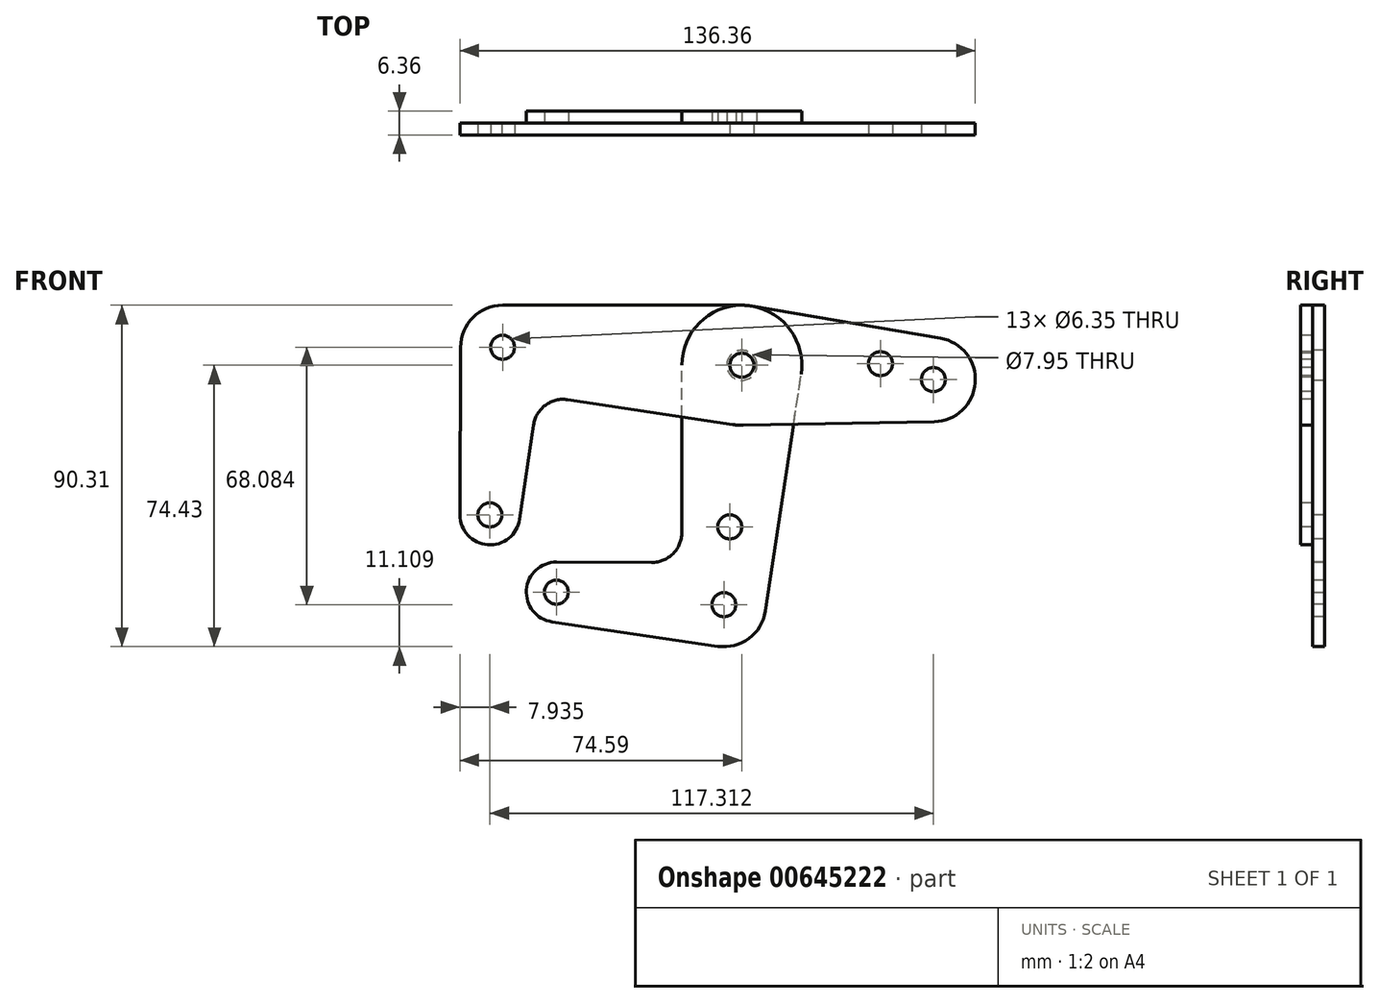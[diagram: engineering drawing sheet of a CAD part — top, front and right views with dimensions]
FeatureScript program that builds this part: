
annotation { "Feature Type Name" : "Feature", "Feature Type Description" : "" }
export const myFeature = defineFeature(function(context is Context, id is Id, definition is map)
    precondition{}
    {
        {
            var Q0;
            Q0=qCreatedBy(makeId("Front.planeOp"),FACE);
            var sketch = newSketch(context, id + "F0", { "sketchPlane" : qUnion([Q0])});
            skCircle(sketch, "E0", {"center": v(0, 0) * mm, "radius": 15.88 * mm});
            skCircle(sketch, "E1", {"center": v(-63.32, 4.76) * mm, "radius": 11.11 * mm});
            skCircle(sketch, "E2", {"center": v(-66.65, -39.56) * mm, "radius": 7.94 * mm});
            skCircle(sketch, "E3", {"center": v(50.66, -3.81) * mm, "radius": 11.11 * mm});
            skCircle(sketch, "E4", {"center": v(36.66, 0.43) * mm, "radius": 3.18 * mm});
            skLineSegment(sketch, "E5", {"start": v(-116.82, 8.79) * mm, "end": v(50.66, -3.81) * mm, "construction": true});
            skLineSegment(sketch, "E6", {"start": v(0, 0) * mm, "end": v(7.45, 99.05) * mm, "construction": true});
            skCircle(sketch, "E7", {"center": v(50.66, -3.81) * mm, "radius": 3.18 * mm});
            skCircle(sketch, "E8", {"center": v(0, 0) * mm, "radius": 3.98 * mm});
            skCircle(sketch, "E9", {"center": v(0, 0) * mm, "radius": 3.18 * mm});
            skCircle(sketch, "E10", {"center": v(-66.65, -39.56) * mm, "radius": 3.18 * mm});
            skCircle(sketch, "E11", {"center": v(-63.32, 4.76) * mm, "radius": 3.18 * mm});
            skLineSegment(sketch, "E12", {"start": v(36.66, 0.43) * mm, "end": v(87, -3.36) * mm, "construction": true});
            skLineSegment(sketch, "E13", {"start": v(-74.6, -39.53) * mm, "end": v(-74.43, 4.8) * mm});
            skLineSegment(sketch, "E14", {"start": v(-58.8, -40.72) * mm, "end": v(-55.12, -15.79) * mm});
            skLineSegment(sketch, "E15", {"start": v(-66.65, -39.56) * mm, "end": v(-63.32, 4.76) * mm, "construction": true});
            skLineSegment(sketch, "E16", {"start": v(-63.32, 15.88) * mm, "end": v(0, 15.88) * mm});
            skLineSegment(sketch, "E17", {"start": v(-2.37, -15.7) * mm, "end": v(-46.07, -9.09) * mm});
            skLineSegment(sketch, "E18", {"start": v(0.3, -15.87) * mm, "end": v(50.87, -14.92) * mm});
            skLineSegment(sketch, "E19", {"start": v(2.67, 15.65) * mm, "end": v(52.53, 7.14) * mm});
            skArc(sketch, "E20.filletArc", {"start": v(-46.07, -9.09) * mm, "mid": v(-51.99, -10.56) * mm, "end": v(-55.12, -15.79) * mm});
            skLineSegment(sketch, "E21", {"start": v(0, 0) * mm, "end": v(-6.43, -85.46) * mm, "construction": true});
            skLineSegment(sketch, "E22", {"start": v(-49.09, -59.99) * mm, "end": v(42.67, -66.89) * mm, "construction": true});
            skCircle(sketch, "E23", {"center": v(-3.21, -42.73) * mm, "radius": 3.18 * mm});
            skCircle(sketch, "E24", {"center": v(-4.76, -63.32) * mm, "radius": 11.11 * mm});
            skCircle(sketch, "E25", {"center": v(-49.09, -59.99) * mm, "radius": 7.94 * mm});
            skCircle(sketch, "E26", {"center": v(-49.09, -59.99) * mm, "radius": 3.18 * mm});
            skCircle(sketch, "E27", {"center": v(-4.76, -63.32) * mm, "radius": 3.18 * mm});
            skLineSegment(sketch, "E28", {"start": v(6.22, -64.98) * mm, "end": v(15.7, -2.37) * mm});
            skLineSegment(sketch, "E29", {"start": v(-50.25, -67.84) * mm, "end": v(-6.39, -74.31) * mm});
            skLineSegment(sketch, "E30", {"start": v(-49.06, -52.05) * mm, "end": v(-23.85, -52.14) * mm});
            skLineSegment(sketch, "E31", {"start": v(-15.88, -44.2) * mm, "end": v(-15.88, 0) * mm});
            skArc(sketch, "E32.filletArc", {"start": v(-23.85, -52.14) * mm, "mid": v(-18.21, -49.82) * mm, "end": v(-15.88, -44.2) * mm});
            skSolve(sketch);
        }
        {
            var Q0;
            {var subQ0=sQuery(id+"F0.wireOp",EDGE,"E13");Q0=makeQuery(id+"F0.imprint","IMPRINT",FACE,{"disambiguationData":[TD([[makeQuery(id+"F0.imprint","IMPRINT",EDGE,{"derivedFrom":subQ0}),-1.0]])]});}
            var Q1;
            Q1=makeQuery(id+"F0.imprint","IMPRINT",FACE,{"disambiguationData":[TD([[makeQuery(id+"F0.imprint","IMPRINT",EDGE,{"derivedFrom":sQuery(id+"F0.wireOp",EDGE,"E4")}),-1.0]])]});
            var Q2;
            {var subQ0=sQuery(id+"F0.wireOp",EDGE,"E18");var subQ1=sQuery(id+"F0.wireOp",EDGE,"E0");var subQ2=makeQuery(id+"F0.imprint","INTERSECT",VERTEX,{"derivedFrom":[subQ1,subQ0]});Q2=makeQuery(id+"F0.imprint","IMPRINT",FACE,{"disambiguationData":[TD([[makeQuery(id+"F0.imprint","IMPRINT",EDGE,{"disambiguationData":[TD([[subQ2,-1.0]])],"derivedFrom":subQ1}),-1.0]])]});}
            var Q3;
            {var subQ0=sQuery(id+"F0.wireOp",EDGE,"E17");var subQ1=sQuery(id+"F0.wireOp",EDGE,"E0");var subQ2=makeQuery(id+"F0.imprint","INTERSECT",VERTEX,{"derivedFrom":[subQ1,subQ0]});Q3=makeQuery(id+"F0.imprint","IMPRINT",FACE,{"disambiguationData":[TD([[makeQuery(id+"F0.imprint","IMPRINT",EDGE,{"disambiguationData":[TD([[subQ2,1.0]])],"derivedFrom":subQ1}),-1.0]])]});}
            var Q4;
            Q4=makeQuery(id+"F0.imprint","IMPRINT",FACE,{"disambiguationData":[TD([[makeQuery(id+"F0.imprint","IMPRINT",EDGE,{"derivedFrom":sQuery(id+"F0.wireOp",EDGE,"E8")}),-1.0]])]});
            var Q5;
            Q5=makeQuery(id+"F0.imprint","IMPRINT",FACE,{"disambiguationData":[TD([[makeQuery(id+"F0.imprint","IMPRINT",EDGE,{"derivedFrom":sQuery(id+"F0.wireOp",EDGE,"E8")}),1.0]])]});
            var Q6;
            Q6=makeQuery(id+"F0.imprint","IMPRINT",FACE,{"disambiguationData":[TD([[makeQuery(id+"F0.imprint","IMPRINT",EDGE,{"derivedFrom":sQuery(id+"F0.wireOp",EDGE,"E10")}),-1.0]])]});
            var Q7;
            Q7=makeQuery(id+"F0.imprint","IMPRINT",FACE,{"disambiguationData":[TD([[makeQuery(id+"F0.imprint","IMPRINT",EDGE,{"derivedFrom":sQuery(id+"F0.wireOp",EDGE,"E11")}),-1.0]])]});
            var Q8;
            Q8=makeQuery(id+"F0.imprint","IMPRINT",FACE,{"disambiguationData":[TD([[makeQuery(id+"F0.imprint","IMPRINT",EDGE,{"derivedFrom":sQuery(id+"F0.wireOp",EDGE,"E7")}),-1.0]])]});
            extrude(context, id + "F1", {"entities" : qUnion([Q0, Q1, Q2, Q3, Q4, Q5, Q6, Q7, Q8]), "depth" : 3.17 * mm, "offsetDistance" : 25.4 * mm});
        }
        {
            var Q0;
            Q0=makeQuery(id+"F0.imprint","IMPRINT",FACE,{"disambiguationData":[TD([[makeQuery(id+"F0.imprint","IMPRINT",EDGE,{"derivedFrom":sQuery(id+"F0.wireOp",EDGE,"E23")}),-1.0]])]});
            var Q1;
            Q1=makeQuery(id+"F0.imprint","IMPRINT",FACE,{"disambiguationData":[TD([[makeQuery(id+"F0.imprint","IMPRINT",EDGE,{"derivedFrom":sQuery(id+"F0.wireOp",EDGE,"E26")}),-1.0]])]});
            var Q2;
            Q2=makeQuery(id+"F1.opExtrude","CAP_FACE",FACE,{"disambiguationData":[OSD([sQuery(id+"F0.wireOp",EDGE,"E0"),sQuery(id+"F0.wireOp",EDGE,"E1"),sQuery(id+"F0.wireOp",EDGE,"E2"),sQuery(id+"F0.wireOp",EDGE,"E3"),sQuery(id+"F0.wireOp",EDGE,"E4"),sQuery(id+"F0.wireOp",EDGE,"E7"),sQuery(id+"F0.wireOp",EDGE,"E9"),sQuery(id+"F0.wireOp",EDGE,"E10"),sQuery(id+"F0.wireOp",EDGE,"E11"),sQuery(id+"F0.wireOp",EDGE,"E13"),sQuery(id+"F0.wireOp",EDGE,"E14"),sQuery(id+"F0.wireOp",EDGE,"E16"),sQuery(id+"F0.wireOp",EDGE,"E17"),sQuery(id+"F0.wireOp",EDGE,"E18"),sQuery(id+"F0.wireOp",EDGE,"E19"),sQuery(id+"F0.wireOp",EDGE,"E20.filletArc")])],"isStart":false});
            var Q3;
            {var subQ0=sQuery(id+"F0.wireOp",EDGE,"E18");var subQ1=sQuery(id+"F0.wireOp",EDGE,"E0");var subQ2=makeQuery(id+"F0.imprint","INTERSECT",VERTEX,{"derivedFrom":[subQ1,subQ0]});Q3=makeQuery(id+"F0.imprint","IMPRINT",FACE,{"disambiguationData":[TD([[makeQuery(id+"F0.imprint","IMPRINT",EDGE,{"disambiguationData":[TD([[subQ2,-1.0]])],"derivedFrom":subQ1}),-1.0]])]});}
            var Q4;
            {var subQ0=sQuery(id+"F0.wireOp",EDGE,"E17");var subQ1=sQuery(id+"F0.wireOp",EDGE,"E0");var subQ2=makeQuery(id+"F0.imprint","INTERSECT",VERTEX,{"derivedFrom":[subQ1,subQ0]});Q4=makeQuery(id+"F0.imprint","IMPRINT",FACE,{"disambiguationData":[TD([[makeQuery(id+"F0.imprint","IMPRINT",EDGE,{"disambiguationData":[TD([[subQ2,1.0]])],"derivedFrom":subQ1}),-1.0]])]});}
            var Q5;
            Q5=makeQuery(id+"F0.imprint","IMPRINT",FACE,{"disambiguationData":[TD([[makeQuery(id+"F0.imprint","IMPRINT",EDGE,{"derivedFrom":sQuery(id+"F0.wireOp",EDGE,"E27")}),-1.0]])]});
            var Q6;
            Q6=makeQuery(id+"F0.imprint","IMPRINT",FACE,{"disambiguationData":[TD([[makeQuery(id+"F0.imprint","IMPRINT",EDGE,{"derivedFrom":sQuery(id+"F0.wireOp",EDGE,"E8")}),-1.0]])]});
            extrude(context, id + "F2", {"entities" : qUnion([Q0, Q1, Q2, Q3, Q4, Q5, Q6]), "oppositeDirection" : true, "depth" : 3.17 * mm, "offsetDistance" : 25.4 * mm});
        }
    });
